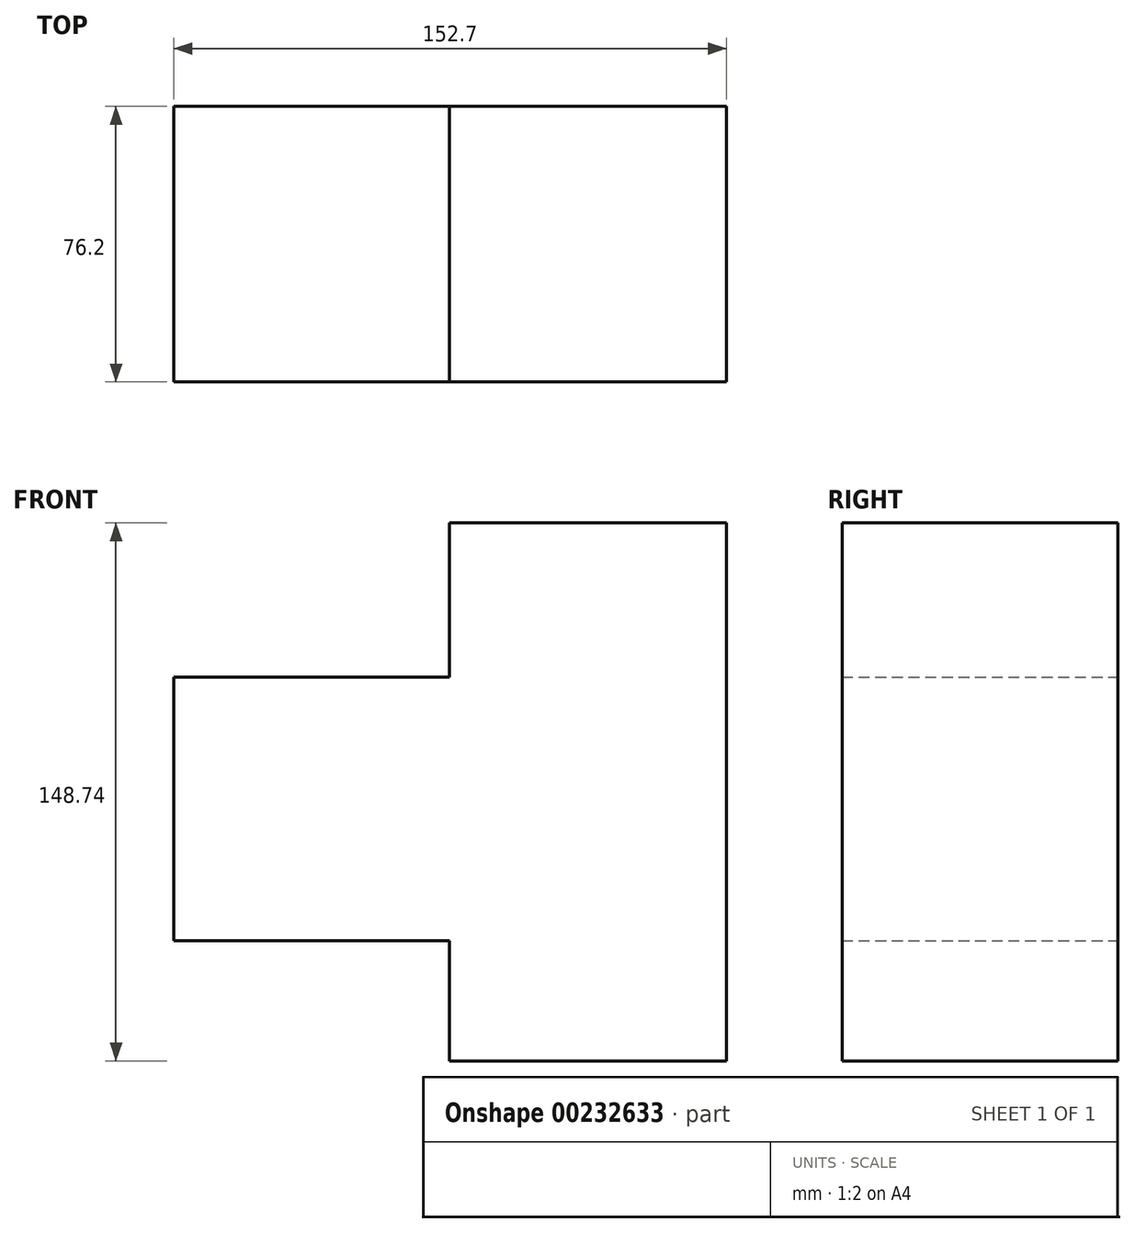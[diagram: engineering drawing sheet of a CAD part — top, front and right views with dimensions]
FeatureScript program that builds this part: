
annotation { "Feature Type Name" : "Feature", "Feature Type Description" : "" }
export const myFeature = defineFeature(function(context is Context, id is Id, definition is map)
    precondition{}
    {
        {
            var Q0;
            Q0=qCreatedBy(makeId("Front.planeOp"),FACE);
            var sketch = newSketch(context, id + "F0", { "sketchPlane" : qUnion([Q0])});
            skLineSegment(sketch, "E0.bottom", {"start": v(0, 74.83) * mm, "end": v(76.5, 74.83) * mm});
            skLineSegment(sketch, "E0.top", {"start": v(0, -73.91) * mm, "end": v(76.5, -73.91) * mm});
            skLineSegment(sketch, "E0.left", {"start": v(0, 74.83) * mm, "end": v(0, -73.91) * mm});
            skLineSegment(sketch, "E0.right", {"start": v(76.5, 74.83) * mm, "end": v(76.5, -73.91) * mm});
            skLineSegment(sketch, "E1.bottom", {"start": v(0, 32.16) * mm, "end": v(-76.2, 32.16) * mm});
            skLineSegment(sketch, "E1.top", {"start": v(0, -40.7) * mm, "end": v(-76.2, -40.7) * mm});
            skLineSegment(sketch, "E1.left", {"start": v(0, 32.16) * mm, "end": v(0, -40.7) * mm});
            skLineSegment(sketch, "E1.right", {"start": v(-76.2, 32.16) * mm, "end": v(-76.2, -40.7) * mm});
            skSolve(sketch);
        }
        {
            var Q0;
            {var subQ3=sQuery(id+"F0.wireOp",EDGE,"E0.bottom");Q0=makeQuery(id+"F0.imprint","IMPRINT",FACE,{"disambiguationData":[TD([[makeQuery(id+"F0.imprint","IMPRINT",EDGE,{"derivedFrom":subQ3}),-1.0]])]});}
            var Q1;
            Q1=makeQuery(id+"F0.imprint","IMPRINT",FACE,{"disambiguationData":[TD([[makeQuery(id+"F0.imprint","IMPRINT",EDGE,{"derivedFrom":sQuery(id+"F0.wireOp",EDGE,"E1.bottom")}),1.0]])]});
            extrude(context, id + "F1", {"entities" : qUnion([Q0, Q1]), "depth" : 76.2 * mm});
        }
    });
